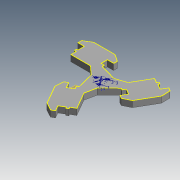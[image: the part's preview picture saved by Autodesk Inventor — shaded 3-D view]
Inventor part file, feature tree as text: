
AUTODESK INVENTOR PART (.ipt)
format: ipt  version: 2014 SP1 (Build 180222100, 222)  size: 187,904 bytes
history: native  units: in
note: dims shown in document units (in); Inventor stores cm internally (conversion verified against a paired STEP export)
features: extrude x2, plane x1, pattern_circular x1, sketch x1
ambient origin geometry x8: Origin, YZ Plane, XZ Plane, XY Plane, X Axis, Y Axis, Z Axis, Center Point
bodies: Solid1 (feature_tree)
feature tree (5):
  plane  "Work Plane3"
  extrude  "Extrusion1"  Depth=0.2835in
  pattern_circular  "Circular Pattern2"  [2 undecoded]
  extrude  "Extrusion2"  Depth=0.1181in
  sketch  "Sketch2"  dims[d1=1.0472in d4=0.2835in d5=0.1028in d6=0.1181in d7=0.0787in d8=0.3409in d9=0.3409in d10=0.1969in d11=0.3409in d12=1.2472in d13=0.1736in d14=0.1148in d17=0.3409in d18=1.15in d20=0.4043in d21=0.1969in d22=0.9126in d23=0.5169in d26=0.3409in d27=0.0in d31=0.5169in d32=1.1811in d33=360.0deg d35=0.1181in d36=0.5512in d37=0.1181in d38=0.1181in d39=0.1181in d40=0.3937in d41=0.0in]
note: 2 required parameter values undecoded (feature->parameter linkage not recoverable at this tier; creation-order binding heuristic only, values carry confidence <= 0.55)
